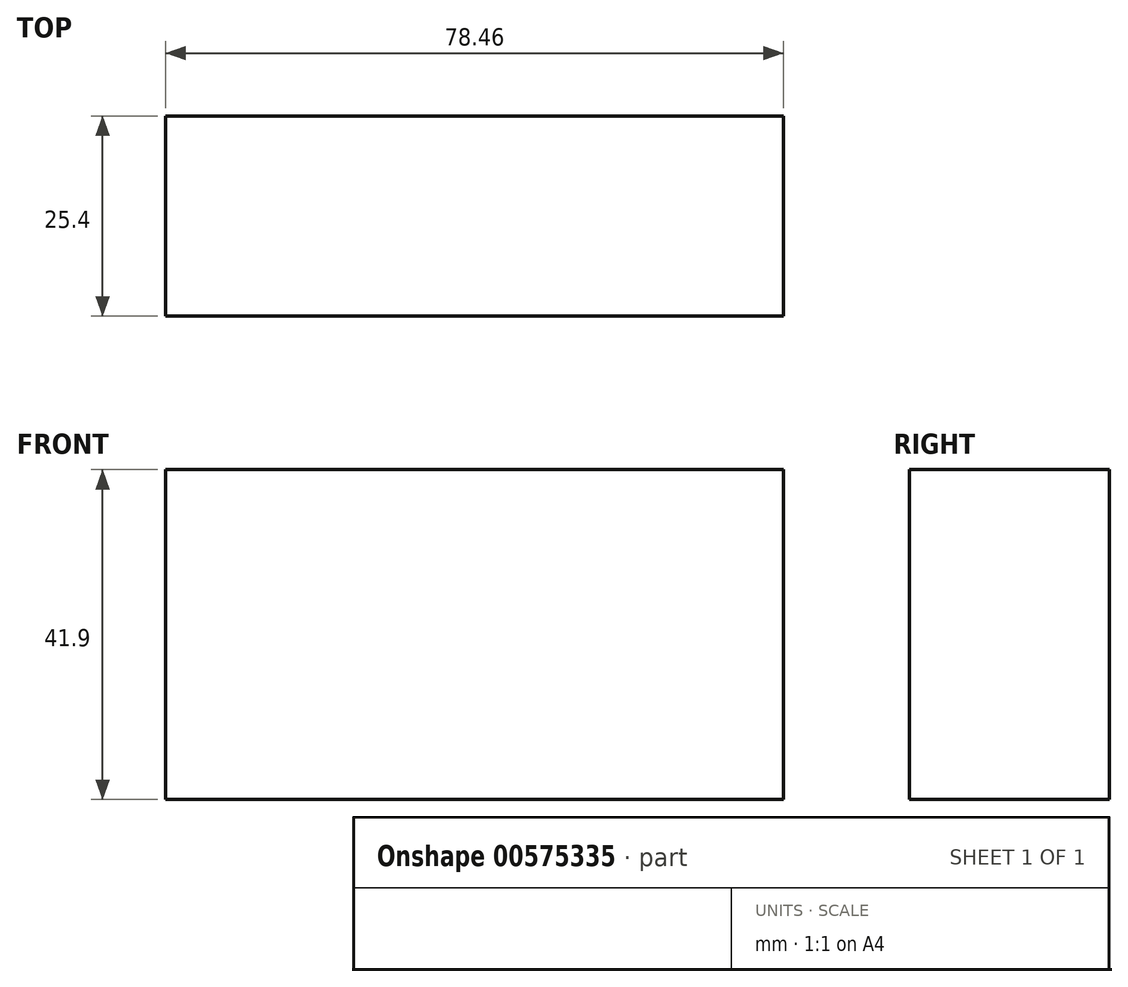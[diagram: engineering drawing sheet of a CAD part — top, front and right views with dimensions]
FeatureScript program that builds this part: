
annotation { "Feature Type Name" : "Feature", "Feature Type Description" : "" }
export const myFeature = defineFeature(function(context is Context, id is Id, definition is map)
    precondition{}
    {
        {
            var Q0;
            Q0=qCreatedBy(makeId("Front.planeOp"),FACE);
            var sketch = newSketch(context, id + "F0", { "sketchPlane" : qUnion([Q0])});
            skLineSegment(sketch, "E0.bottom", {"start": v(39.23, -20.95) * mm, "end": v(-39.23, -20.95) * mm});
            skLineSegment(sketch, "E0.top", {"start": v(39.23, 20.95) * mm, "end": v(-39.23, 20.95) * mm});
            skLineSegment(sketch, "E0.left", {"start": v(39.23, -20.95) * mm, "end": v(39.23, 20.95) * mm});
            skLineSegment(sketch, "E0.right", {"start": v(-39.23, -20.95) * mm, "end": v(-39.23, 20.95) * mm});
            skPoint(sketch, "E0.middle", {"position": v(0, 0) * mm});
            skSolve(sketch);
        }
        {
            var Q0;
            Q0=makeQuery(id+"F0.imprint","IMPRINT",FACE,{"disambiguationData":[TD([[makeQuery(id+"F0.imprint","IMPRINT",EDGE,{"derivedFrom":sQuery(id+"F0.wireOp",EDGE,"E0.bottom")}),-1.0]])]});
            extrude(context, id + "F1", {"entities" : qUnion([Q0]), "depth" : 25.4 * mm, "offsetDistance" : 25.4 * mm});
        }
    });
